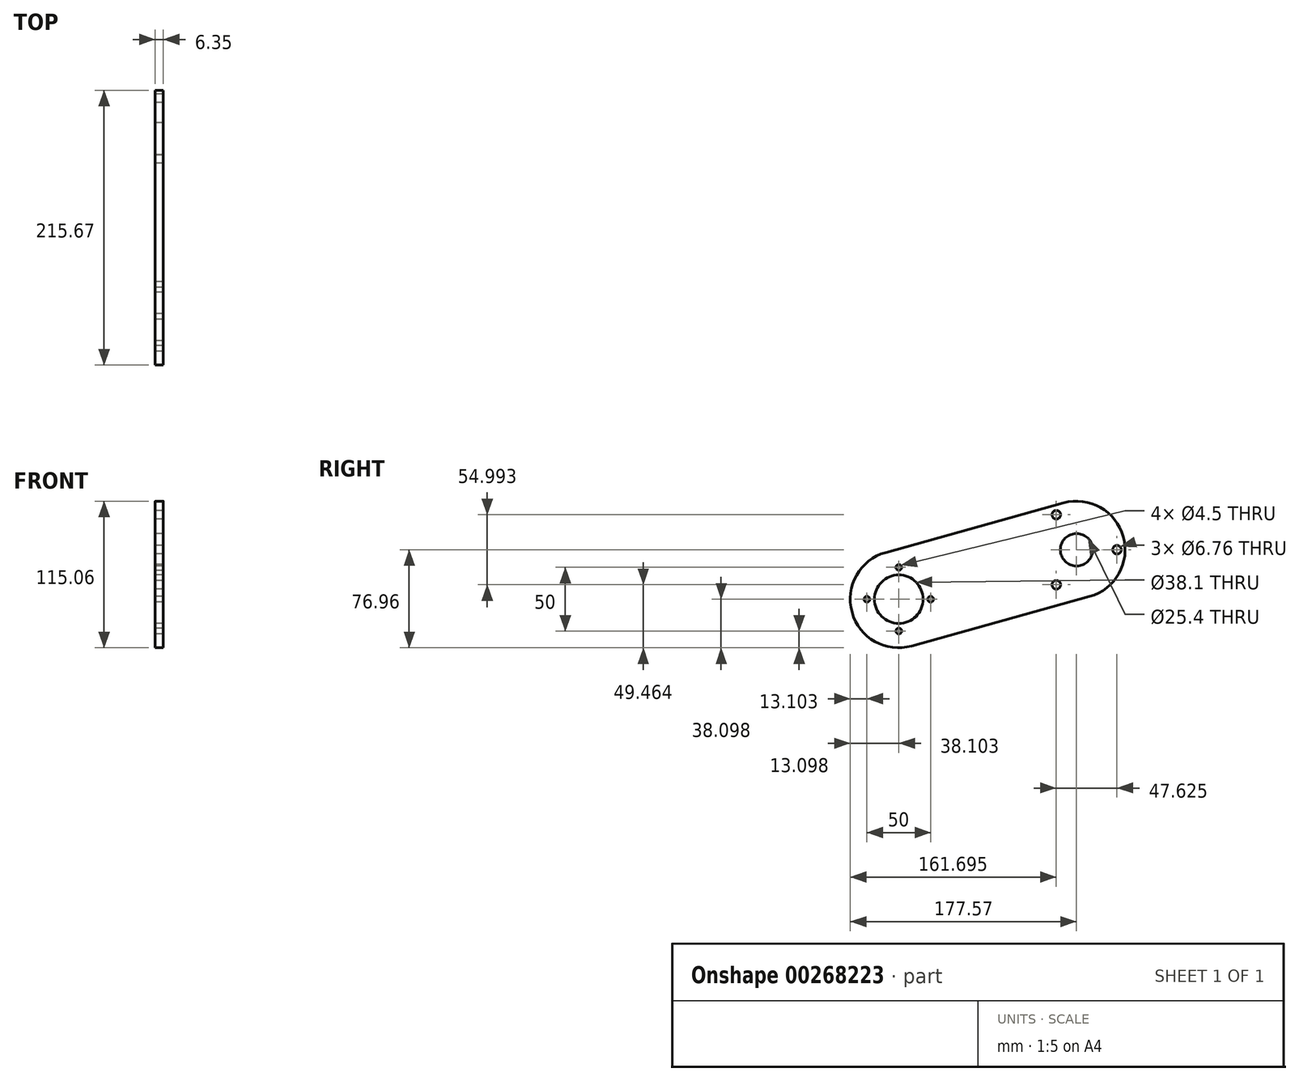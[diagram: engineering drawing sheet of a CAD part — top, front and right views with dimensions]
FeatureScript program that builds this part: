
annotation { "Feature Type Name" : "Feature", "Feature Type Description" : "" }
export const myFeature = defineFeature(function(context is Context, id is Id, definition is map)
    precondition{}
    {
        {
            var Q0;
            Q0=qCreatedBy(makeId("Right.planeOp"),FACE);
            var sketch = newSketch(context, id + "F0", { "sketchPlane" : qUnion([Q0])});
            skLineSegment(sketch, "E0", {"start": v(-189.76, 0) * mm, "end": v(0, 0) * mm, "construction": true});
            skCircle(sketch, "E1", {"center": v(-139.47, -38.86) * mm, "radius": 38.86 * mm, "construction": true});
            skArc(sketch, "E2", {"start": v(10.23, -36.7) * mm, "mid": v(36.7, 10.23) * mm, "end": v(-10.23, 36.7) * mm});
            skLineSegment(sketch, "E3", {"start": v(-184.34, -114.3) * mm, "end": v(143.24, -114.3) * mm, "construction": true});
            skCircle(sketch, "E4", {"center": v(0, 0) * mm, "radius": 95.25 * mm, "construction": true});
            skCircle(sketch, "E5", {"center": v(0, 0) * mm, "radius": 31.75 * mm, "construction": true});
            skCircle(sketch, "E6.2.0", {"center": v(31.75, 0) * mm, "radius": 3.18 * mm, "construction": true});
            skCircle(sketch, "E7", {"center": v(-139.47, -38.86) * mm, "radius": 25 * mm, "construction": true});
            skCircle(sketch, "E8", {"center": v(-139.47, -13.86) * mm, "radius": 2.08 * mm, "construction": true});
            skCircle(sketch, "E9", {"center": v(-139.47, -63.86) * mm, "radius": 2.08 * mm, "construction": true});
            skCircle(sketch, "E10", {"center": v(-114.47, -38.86) * mm, "radius": 2.08 * mm, "construction": true});
            skCircle(sketch, "E11", {"center": v(-164.47, -38.86) * mm, "radius": 2.08 * mm, "construction": true});
            skArc(sketch, "E12", {"start": v(-149.7, -2.16) * mm, "mid": v(-176.17, -49.09) * mm, "end": v(-129.24, -75.56) * mm});
            skLineSegment(sketch, "E13", {"start": v(-149.7, -2.16) * mm, "end": v(-10.23, 36.7) * mm});
            skLineSegment(sketch, "E14.trimOffspring", {"start": v(-129.24, -75.56) * mm, "end": v(10.23, -36.7) * mm});
            skLineSegment(sketch, "E15", {"start": v(0, 0) * mm, "end": v(-15.88, 27.5) * mm, "construction": true});
            skLineSegment(sketch, "E16", {"start": v(0, 0) * mm, "end": v(-15.87, -27.5) * mm, "construction": true});
            skCircle(sketch, "E17", {"center": v(-15.87, -27.5) * mm, "radius": 3.18 * mm, "construction": true});
            skCircle(sketch, "E18", {"center": v(-15.88, 27.5) * mm, "radius": 3.18 * mm, "construction": true});
            skLineSegment(sketch, "E19", {"start": v(0, 0) * mm, "end": v(31.75, 0) * mm, "construction": true});
            skCircle(sketch, "E20", {"center": v(-139.47, -38.86) * mm, "radius": 19.05 * mm});
            skCircle(sketch, "E21", {"center": v(0, 0) * mm, "radius": 12.7 * mm});
            skSolve(sketch);
        }
        {
            var Q0;
            Q0 = qSketchRegion(id + "F0", true);
            extrude(context, id + "F1", {"entities" : qUnion([Q0]), "depth" : 6.35 * mm});
        }
        {
            var Q0;
            Q0=sQuery(id+"F0.wireOp",VERTEX,"E8.center");
            var Q1;
            Q1=sQuery(id+"F0.wireOp",VERTEX,"E11.center");
            var Q2;
            Q2=sQuery(id+"F0.wireOp",VERTEX,"E10.center");
            var Q3;
            Q3=sQuery(id+"F0.wireOp",VERTEX,"E9.center");
            var Q4;
            Q4=makeQuery(id+"F1.opExtrude","SWEPT_BODY",BODY,{"disambiguationData":[OSD([sQuery(id+"F0.wireOp",EDGE,"E2"),sQuery(id+"F0.wireOp",EDGE,"E12"),sQuery(id+"F0.wireOp",EDGE,"E13"),sQuery(id+"F0.wireOp",EDGE,"E14.trimOffspring")])]});
            hole(context, id + "F2", {"style" : HoleStyle.SIMPLE, "endStyle" : HoleEndStyle.THROUGH, "oppositeDirection" : true, "standardTappedOrClearance" : lookupTablePath({ "standard" : "ANSI", "fit" : "Normal (ASME)", "size" : "#8", "type" : "Clearance" }), "standardBlindInLast" : lookupTablePath({ "fit" : "Free", "standard" : "ANSI", "size" : "#8", "type" : "Clearance" }), "holeDiameter" : 4.5 * mm, "tappedDepth" : 12.7 * mm, "tapClearance" : 3, "startFromSketch" : true, "locations" : qUnion([Q0, Q1, Q2, Q3]), "scope" : qUnion([Q4])});
        }
        {
            var Q0;
            Q0=sQuery(id+"F0.wireOp",VERTEX,"E15.end");
            var Q1;
            Q1=sQuery(id+"F0.wireOp",VERTEX,"E17.center");
            var Q2;
            Q2=sQuery(id+"F0.wireOp",VERTEX,"E6.2.0.center");
            var Q3;
            Q3=makeQuery(id+"F1.opExtrude","SWEPT_BODY",BODY,{"disambiguationData":[OSD([sQuery(id+"F0.wireOp",EDGE,"E2"),sQuery(id+"F0.wireOp",EDGE,"E12"),sQuery(id+"F0.wireOp",EDGE,"E13"),sQuery(id+"F0.wireOp",EDGE,"E14.trimOffspring")])]});
            hole(context, id + "F3", {"style" : HoleStyle.SIMPLE, "endStyle" : HoleEndStyle.THROUGH, "oppositeDirection" : true, "standardTappedOrClearance" : lookupTablePath({ "standard" : "ANSI", "fit" : "Normal (ASME)", "size" : "1/4", "type" : "Clearance" }), "standardBlindInLast" : lookupTablePath({ "fit" : "Free", "standard" : "ANSI", "size" : "1/4", "type" : "Clearance" }), "holeDiameter" : 6.76 * mm, "tappedDepth" : 12.7 * mm, "tapClearance" : 3, "startFromSketch" : true, "locations" : qUnion([Q0, Q1, Q2]), "scope" : qUnion([Q3])});
        }
    });
